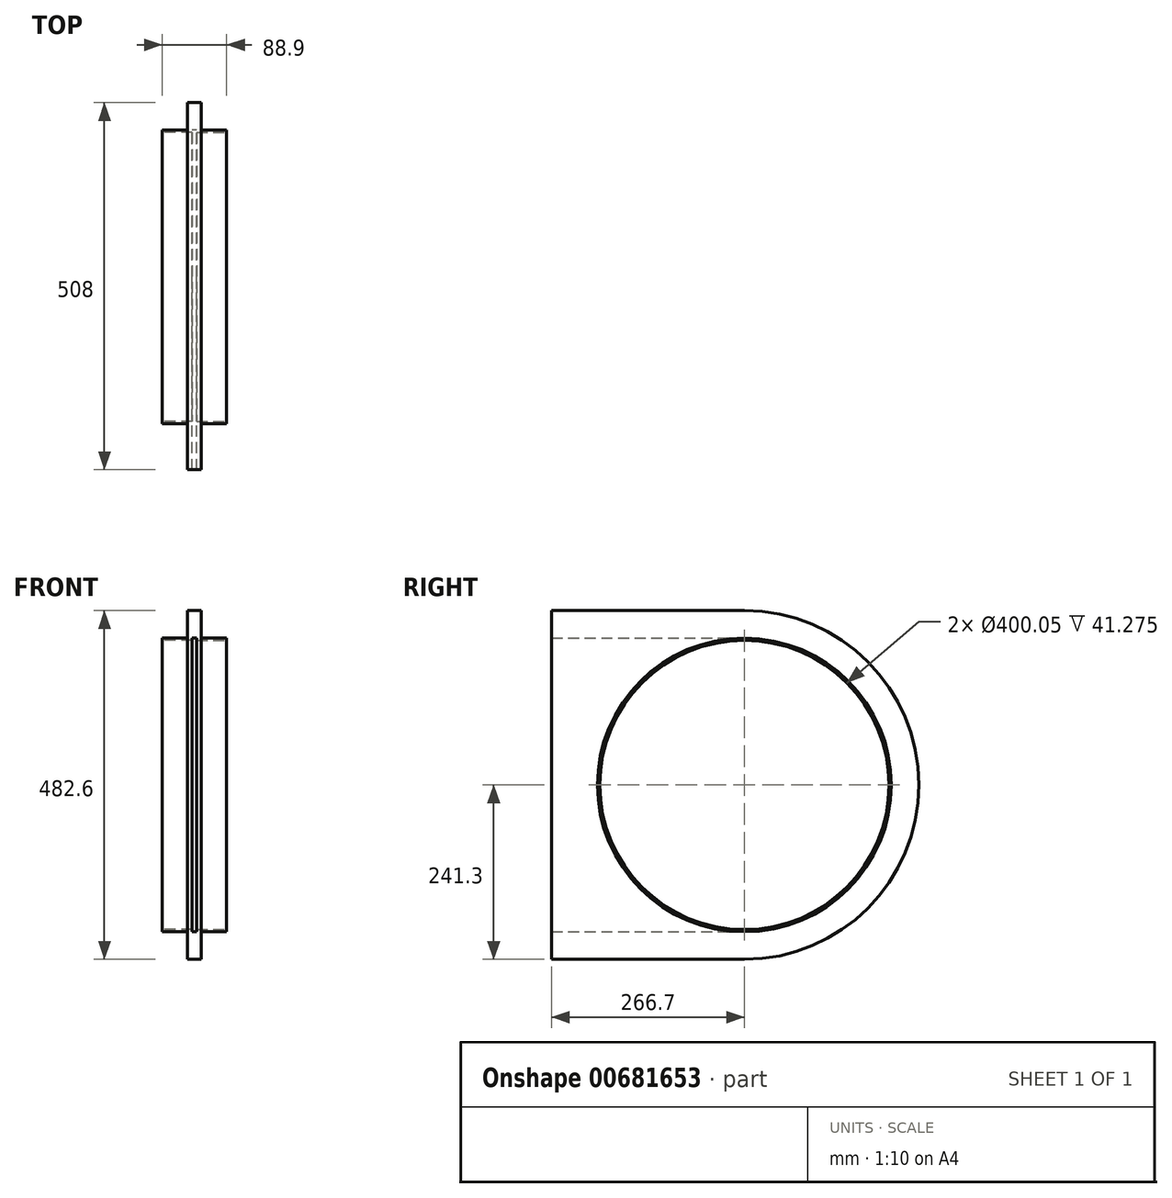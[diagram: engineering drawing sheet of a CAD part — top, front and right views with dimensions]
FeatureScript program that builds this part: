
annotation { "Feature Type Name" : "Feature", "Feature Type Description" : "" }
export const myFeature = defineFeature(function(context is Context, id is Id, definition is map)
    precondition{}
    {
        {
            var Q0;
            Q0=qCreatedBy(makeId("Right.planeOp"),FACE);
            var sketch = newSketch(context, id + "F0", { "sketchPlane" : qUnion([Q0])});
            skCircle(sketch, "E0", {"center": v(0, 0) * mm, "radius": 203.2 * mm});
            skCircle(sketch, "E1", {"center": v(0, 0) * mm, "radius": 200.03 * mm});
            skSolve(sketch);
        }
        {
            var Q0;
            Q0=qCreatedBy(makeId("Top.planeOp"),FACE);
            var sketch = newSketch(context, id + "F1", { "sketchPlane" : qUnion([Q0])});
            skLineSegment(sketch, "E2", {"start": v(0, 0) * mm, "end": v(-88.9, 0) * mm});
            skLineSegment(sketch, "E3", {"start": v(-88.9, 0) * mm, "end": v(-88.9, 203.2) * mm});
            skSolve(sketch);
        }
        {
            var Q0;
            Q0=sQuery(id+"F1.wireOp",EDGE,"E3");
            cPlane(context, id + "F2", {"entities" : qUnion([Q0]), "cplaneType" : CPlaneType.LINE_ANGLE, "offset" : 25.4 * mm, "angle" : 90 * degree, "width" : 152.4 * mm, "height" : 152.4 * mm});
        }
        {
            var Q0;
            Q0=qCreatedBy(id+"F2.planeOp",FACE);
            var sketch = newSketch(context, id + "F3", { "sketchPlane" : qUnion([Q0])});
            skCircle(sketch, "E4", {"center": v(0, 0) * mm, "radius": 203.2 * mm});
            skCircle(sketch, "E5", {"center": v(0, 0) * mm, "radius": 200.03 * mm});
            skSolve(sketch);
        }
        {
            var Q0;
            Q0 = qSketchRegion(id + "F3", true);
            extrude(context, id + "F4", {"entities" : qUnion([Q0]), "depth" : 34.92 * mm, "offsetDistance" : 25.4 * mm});
        }
        {
            var Q0;
            Q0=makeQuery(id+"F0.imprint","IMPRINT",FACE,{"disambiguationData":[TD([[makeQuery(id+"F0.imprint","IMPRINT",EDGE,{"derivedFrom":sQuery(id+"F0.wireOp",EDGE,"E0")}),1.0]])]});
            var Q1;
            Q1=sQuery(id+"F0.wireOp",EDGE,"E1");
            var Q2;
            Q2=sQuery(id+"F0.wireOp",EDGE,"E0");
            extrude(context, id + "F5", {"entities" : qUnion([Q0]), "surfaceEntities" : qUnion([Q1, Q2]), "oppositeDirection" : true, "depth" : 34.92 * mm, "offsetDistance" : 25.4 * mm});
        }
        {
            var Q0;
            Q0=makeQuery(id+"F4.opExtrude","CAP_FACE",FACE,{"disambiguationData":[OSD([sQuery(id+"F3.wireOp",EDGE,"E4"),sQuery(id+"F3.wireOp",EDGE,"E5")])],"isStart":false});
            cPlane(context, id + "F6", {"entities" : qUnion([Q0]), "cplaneType" : CPlaneType.OFFSET, "offset" : 0 * mm, "width" : 152.4 * mm, "height" : 152.4 * mm});
        }
        {
            var Q0;
            Q0=qCreatedBy(id+"F6.planeOp",FACE);
            var sketch = newSketch(context, id + "F7", { "sketchPlane" : qUnion([Q0])});
            skLineSegment(sketch, "E6", {"start": v(0, 0) * mm, "end": v(-266.7, 0) * mm, "construction": true});
            skLineSegment(sketch, "E7", {"start": v(-266.7, 0) * mm, "end": v(-266.7, 241.3) * mm, "construction": true});
            skCircle(sketch, "E8", {"center": v(0, 0) * mm, "radius": 200.03 * mm});
            skCircle(sketch, "E9", {"center": v(0, 0) * mm, "radius": 241.3 * mm});
            skLineSegment(sketch, "E10", {"start": v(0, 241.3) * mm, "end": v(-266.7, 241.3) * mm});
            skLineSegment(sketch, "E11", {"start": v(-266.7, 241.3) * mm, "end": v(-266.7, -241.3) * mm});
            skLineSegment(sketch, "E12", {"start": v(-266.7, -241.3) * mm, "end": v(0, -241.3) * mm});
            skSolve(sketch);
        }
        {
            var Q0;
            {var subQ0=sQuery(id+"F7.wireOp",EDGE,"E10");Q0=makeQuery(id+"F7.imprint","IMPRINT",FACE,{"disambiguationData":[TD([[makeQuery(id+"F7.imprint","IMPRINT",EDGE,{"derivedFrom":subQ0}),1.0]])]});}
            var Q1;
            Q1=makeQuery(id+"F7.imprint","IMPRINT",FACE,{"disambiguationData":[TD([[makeQuery(id+"F7.imprint","IMPRINT",EDGE,{"derivedFrom":sQuery(id+"F7.wireOp",EDGE,"E8")}),-1.0]])]});
            extrude(context, id + "F8", {"entities" : qUnion([Q0, Q1]), "depth" : 6.35 * mm, "offsetDistance" : 25.4 * mm});
        }
        {
            var Q0;
            Q0=makeQuery(id+"F8.opExtrude","CAP_FACE",FACE,{"disambiguationData":[OSD([sQuery(id+"F7.wireOp",EDGE,"E8"),sQuery(id+"F7.wireOp",EDGE,"E9"),sQuery(id+"F7.wireOp",EDGE,"E10"),sQuery(id+"F7.wireOp",EDGE,"E11"),sQuery(id+"F7.wireOp",EDGE,"E12")])],"isStart":false});
            cPlane(context, id + "F9", {"entities" : qUnion([Q0]), "cplaneType" : CPlaneType.OFFSET, "offset" : 3.17 * mm, "width" : 152.4 * mm, "height" : 152.4 * mm});
        }
        {
            var Q0;
            Q0=makeQuery(id+"F8.opExtrude","SWEPT_BODY",BODY,{"disambiguationData":[OSD([sQuery(id+"F7.wireOp",EDGE,"E8"),sQuery(id+"F7.wireOp",EDGE,"E9"),sQuery(id+"F7.wireOp",EDGE,"E10"),sQuery(id+"F7.wireOp",EDGE,"E11"),sQuery(id+"F7.wireOp",EDGE,"E12")])]});
            var Q1;
            Q1=qCreatedBy(id+"F9.planeOp",FACE);
            mirror(context, id + "F10", {"operationType" : NewBodyOperationType.ADD, "entities" : qUnion([Q0]), "mirrorPlane" : qUnion([Q1])});
        }
        {
            var Q0;
            Q0=makeQuery(id+"F8.opExtrude","CAP_FACE",FACE,{"disambiguationData":[OSD([sQuery(id+"F7.wireOp",EDGE,"E8"),sQuery(id+"F7.wireOp",EDGE,"E9"),sQuery(id+"F7.wireOp",EDGE,"E10"),sQuery(id+"F7.wireOp",EDGE,"E11"),sQuery(id+"F7.wireOp",EDGE,"E12")])],"isStart":false});
            cPlane(context, id + "F11", {"entities" : qUnion([Q0]), "cplaneType" : CPlaneType.OFFSET, "offset" : 0 * mm, "width" : 152.4 * mm, "height" : 152.4 * mm});
        }
        {
            var Q0;
            Q0=qCreatedBy(id+"F11.planeOp",FACE);
            var sketch = newSketch(context, id + "F12", { "sketchPlane" : qUnion([Q0])});
            skArc(sketch, "E13", {"start": v(0, 203.2) * mm, "mid": v(203.2, 0) * mm, "end": v(0, -203.2) * mm});
            skArc(sketch, "E14", {"start": v(0, 241.3) * mm, "mid": v(241.3, 0) * mm, "end": v(0, -241.3) * mm});
            skLineSegment(sketch, "E15", {"start": v(0, 241.3) * mm, "end": v(-266.7, 241.3) * mm});
            skLineSegment(sketch, "E16", {"start": v(-266.7, 241.3) * mm, "end": v(-266.7, 203.2) * mm});
            skLineSegment(sketch, "E17", {"start": v(-266.7, 203.2) * mm, "end": v(0, 203.2) * mm});
            skLineSegment(sketch, "E18", {"start": v(0, -241.3) * mm, "end": v(-266.7, -241.3) * mm});
            skLineSegment(sketch, "E19", {"start": v(-266.7, -241.3) * mm, "end": v(-266.7, -203.2) * mm});
            skLineSegment(sketch, "E20", {"start": v(-266.7, -203.2) * mm, "end": v(0, -203.2) * mm});
            skSolve(sketch);
        }
        {
            var Q0;
            Q0 = qSketchRegion(id + "F12", true);
            extrude(context, id + "F13", {"entities" : qUnion([Q0]), "operationType" : NewBodyOperationType.ADD, "depth" : 6.35 * mm, "offsetDistance" : 25.4 * mm});
        }
    });
